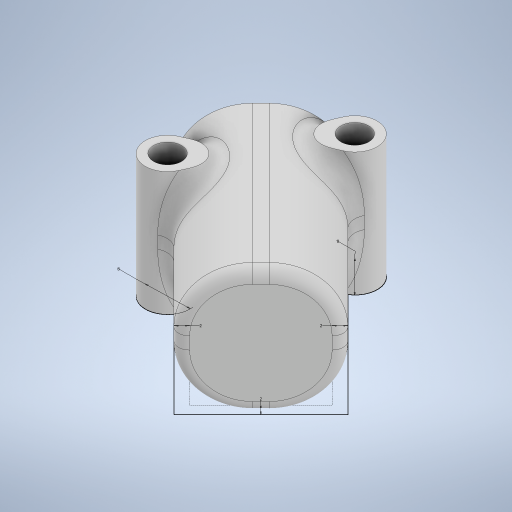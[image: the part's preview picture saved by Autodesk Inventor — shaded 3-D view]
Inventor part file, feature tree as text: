
AUTODESK INVENTOR PART (.ipt)
format: ipt  version: 2023 (Build 270158000, 158)  size: 432,128 bytes
history: native  units: in
note: dims shown in document units (in); Inventor stores cm internally (conversion verified against a paired STEP export)
features: extrude x3, fillet x3, sketch x2, hole x1, projected_geometry x1
ambient origin geometry x8: Origin, YZ Plane, XZ Plane, XY Plane, X Axis, Y Axis, Z Axis, Center Point
bodies: Solid1 (feature_tree)
feature tree (10):
  sketch  "Sketch1"  dims[d0=0.315in d1=0.315in d2=0.0787in]
  extrude  "Extrusion1"  Depth=0.315in
  fillet  "Fillet1"  Radius=0.0787in
  extrude  "Extrusion2"  Depth=0.1181in
  extrude  "Extrusion3"  Depth=0.1181in TaperAngle=0.0deg
  hole  "Hole1"  [1 undecoded]
  fillet  "Fillet2"  Radius=0.874in
  fillet  "Fillet3"  Radius=0.874in
  sketch  "Sketch2"  dims[d3=0.0787in d4=0.0787in d5=0.874in d6=0.0in d7=0.3937in d8=0.874in d9=0.0in d10=0.874in d11=0.0in d12=0.7244in d13=0.2362in d14=0.1575in d15=0.0787in d16=90.0deg d17=1.378in d18=0.0in d19=0.0787in d20=0.1181in]
  projected_geometry  "Projected Loop1"
note: 1 required parameter value undecoded (feature->parameter linkage not recoverable at this tier; creation-order binding heuristic only, values carry confidence <= 0.55)
